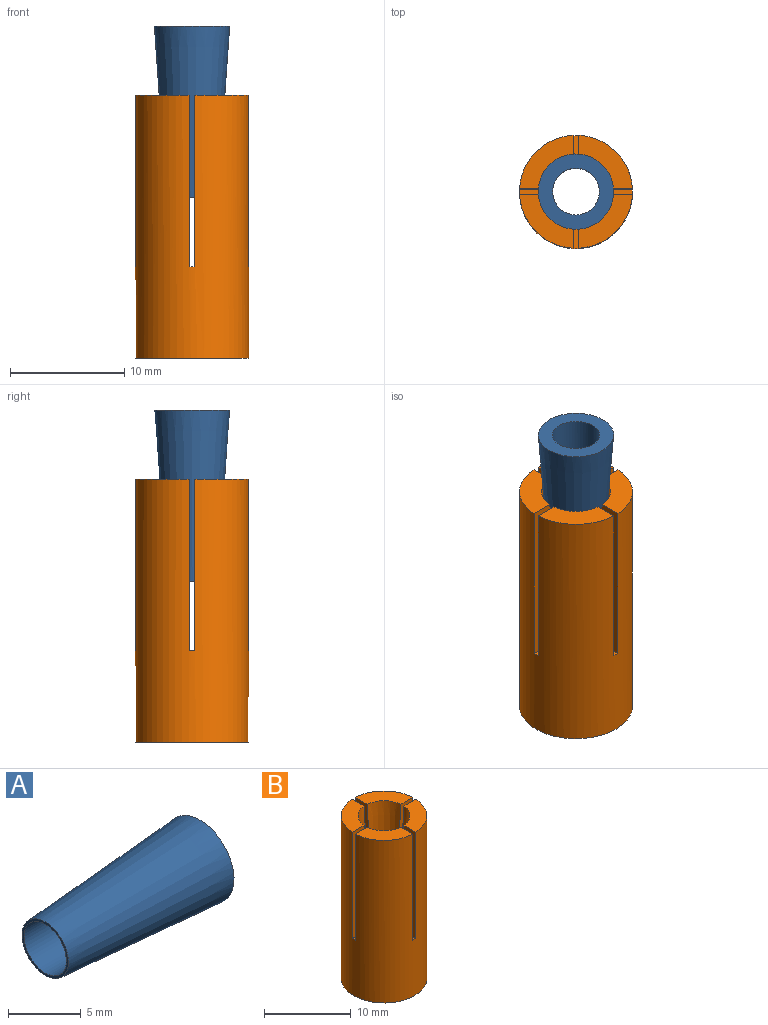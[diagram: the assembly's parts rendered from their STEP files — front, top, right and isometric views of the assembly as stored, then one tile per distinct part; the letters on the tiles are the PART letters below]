
ASSEMBLY  parts=2 mates=1
PART A: 4 faces, bbox 15x6.6x6.6 mm
  f0: plane 4.5x4.5mm, normal (-1,0,0), area 2.7mm2, adj f2,f3
  f1: plane 6.6x6.6mm, normal (1,0,0), area 21mm2, adj f2,f3
  f2: cone r=2.25mm half-angle=4deg, axis (1,0,0), area 262.2mm2, adj f0,f1
  f3: cylinder r=2.05mm len=15mm, axis (-1,0,0), area 193.2mm2, adj f0,f1
PART B: 30 faces, bbox 9.9x9.9x23 mm
  f0: plane 9.9x9.9mm, normal (0,0,-1), area 34.5mm2, adj f5,f23,f24,f25,f26,f27,f28
  f1: cylinder r=2.1mm len=4.5mm, axis (0,0,-1), area 59.4mm2, adj f2,f3,f4,f7,f11,f14,f18,f20
  f2: plane 2.87x0.5mm, normal (0,0,1), area 1.4mm2, adj f1,f5,f9,f13
  f3: plane 2.87x0.5mm, normal (0,0,1), area 1.4mm2, adj f1,f5,f10,f19
  f4: plane 2.87x0.5mm, normal (0,0,1), area 1.4mm2, adj f1,f5,f17,f22
  f5: cylinder r=4.95mm len=23mm, axis (0,0,-1), area 685.3mm2, adj f0,f2,f3,f4,f6,f8,f9,f10
  f6: plane 4.69x4.69mm, normal (0,0,1), area 11.2mm2, adj f5,f7,f8,f9
  f7: cone r=3mm half-angle=3.4deg, axis (0,0,1), area 52.5mm2, adj f1,f6,f8,f9
  f8: plane 15.02x2.87mm, normal (0,1,0), area 36.1mm2, adj f5,f6,f7,f18
  f9: plane 15.02x2.87mm, normal (1,0,0), area 36.1mm2, adj f2,f5,f6,f7
  f10: plane 15.02x2.87mm, normal (0,1,0), area 36.1mm2, adj f3,f5,f11,f12
  f11: cone r=3mm half-angle=3.4deg, axis (0,0,1), area 52.5mm2, adj f1,f10,f12,f13
  f12: plane 4.69x4.69mm, normal (0,0,1), area 11.2mm2, adj f5,f10,f11,f13
  f13: plane 15.02x2.87mm, normal (-1,0,0), area 36.1mm2, adj f2,f5,f11,f12
  f14: cone r=3mm half-angle=3.4deg, axis (0,0,1), area 52.5mm2, adj f1,f15,f16,f17
  f15: plane 4.69x4.69mm, normal (0,0,1), area 11.2mm2, adj f5,f14,f16,f17
  f16: plane 15.02x2.87mm, normal (0,-1,0), area 36.1mm2, adj f5,f14,f15,f18
  f17: plane 15.02x2.87mm, normal (1,0,0), area 36.1mm2, adj f4,f5,f14,f15
  f18: plane 2.87x0.5mm, normal (0,0,1), area 1.4mm2, adj f1,f5,f8,f16
  f19: plane 15.02x2.87mm, normal (0,-1,0), area 36.1mm2, adj f3,f5,f20,f21
  f20: cone r=3mm half-angle=3.4deg, axis (0,0,1), area 52.5mm2, adj f1,f19,f21,f22
  f21: plane 4.69x4.69mm, normal (0,0,1), area 11.2mm2, adj f5,f19,f20,f22
  f22: plane 15.02x2.87mm, normal (-1,0,0), area 36.1mm2, adj f4,f5,f20,f21
  f23: plane 4.04x3.5mm, normal (0,1,0), area 14.1mm2, adj f0,f24,f28,f29
  f24: plane 3.5x3.5mm, normal (0.87,0.5,0), area 14.1mm2, adj f0,f23,f25,f29
  f25: plane 3.5x3.5mm, normal (0.87,-0.5,0), area 14.1mm2, adj f0,f24,f26,f29
  f26: plane 4.04x3.5mm, normal (0,-1,0), area 14.1mm2, adj f0,f25,f27,f29
  f27: plane 3.5x3.5mm, normal (-0.87,-0.5,0), area 14.1mm2, adj f0,f26,f28,f29
  f28: plane 3.5x3.5mm, normal (-0.87,0.5,0), area 14.1mm2, adj f0,f23,f27,f29
  f29: plane 8.08x7mm, normal (0,0,-1), area 28.6mm2, adj f1,f23,f24,f25,f26,f27,f28
PLACE A rot(axis=(0,-1,0),90deg) t=(6,0,9.78)mm
PLACE B rot(axis=(0,1,0),0deg) t=(6,0,3.7)mm
MATE cylindrical B.f1 <-> A.f3  axis (0,0,1) through (6,0,18.7)mm
